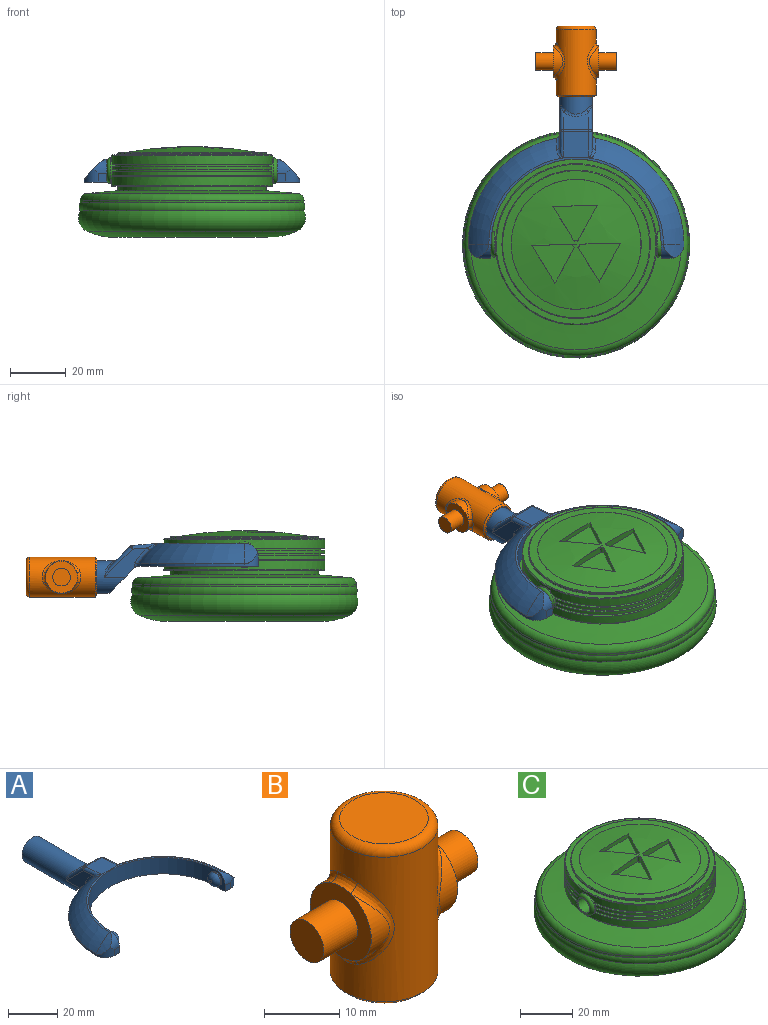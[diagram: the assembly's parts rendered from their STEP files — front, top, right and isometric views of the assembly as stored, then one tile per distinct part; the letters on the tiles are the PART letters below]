
ASSEMBLY  parts=3 mates=2
PART A: 48 faces, bbox 77.3x80.8x18.2 mm
  f0: plane 11.99x9.83mm, normal (0,-0.71,-0.71), area 141.5mm2, adj f1,f2,f9,f30,f43,f46
  f1: plane 15.39x10.49mm, normal (-1,0,0), area 63.5mm2, adj f0,f30,f32,f36,f46,f47
  f2: plane 15.39x10.49mm, normal (1,0,0), area 63.5mm2, adj f0,f30,f34,f39,f43,f44
  f3: plane 9.14x6.37mm, normal (0,0.71,0.71), area 67.6mm2, adj f35,f36,f39,f40
  f4: cylinder r=38.61mm len=37.99mm, axis (0,0,-1), area 42.6mm2, adj f6,f9,f17,f46,f47
  f5: torus R=19.3mm, axis (0,0,-1), area 507.8mm2, adj f10,f11,f12,f29,f42,f44
  f6: torus R=19.3mm, axis (0,0,-1), area 507.8mm2, adj f4,f11,f15,f28,f45,f47
  f7: cylinder r=30.48mm len=60.96mm, axis (0,0,-1), area 746.6mm2, adj f8,f9,f11,f14,f21,f24
  f8: plane 8.13x5.08mm, normal (-1,0,0), area 19.9mm2, adj f7,f9,f13,f19,f24
  f9: plane 77.22x43.73mm, normal (0,0,-1), area 956.2mm2, adj f0,f4,f7,f8,f10,f13,f14,f16
  f10: cylinder r=38.61mm len=37.99mm, axis (0,0,-1), area 42.6mm2, adj f5,f9,f20,f43,f44
  f11: plane 62.55x30.95mm, normal (0,0,1), area 75mm2, adj f5,f6,f7,f18,f19,f27
  f12: cylinder r=22.71mm len=7.33mm, axis (0,1,0), area 24.8mm2, adj f5,f19,f20
  f13: plane 3.05x3.05mm, normal (0,-1,0), area 9.3mm2, adj f8,f9,f19,f20
  f14: plane 8.13x5.08mm, normal (1,0,0), area 19.9mm2, adj f7,f9,f16,f18,f21
  f15: cylinder r=22.71mm len=7.33mm, axis (0,1,0), area 24.8mm2, adj f6,f17,f18
  f16: plane 3.05x3.05mm, normal (0,-1,0), area 9.3mm2, adj f9,f14,f17,f18
  f17: cylinder r=5.08mm len=5.08mm, axis (0,0,-1), area 21.9mm2, adj f4,f9,f15,f16,f18
  f18: cylinder r=5.08mm len=5.08mm, axis (-1,0,0), area 21.9mm2, adj f11,f14,f15,f16,f17
  f19: cylinder r=5.08mm len=5.08mm, axis (-1,0,0), area 21.9mm2, adj f8,f11,f12,f13,f20
  f20: cylinder r=5.08mm len=5.08mm, axis (0,0,-1), area 21.9mm2, adj f9,f10,f12,f13,f19
  f21: cylinder r=3.17mm len=6.35mm, axis (-1,0,0), area 12.7mm2, adj f7,f14,f23
  f22: plane 1.27x1.27mm, normal (1,0,0), area 1.3mm2, adj f23
  f23: torus R=0.64mm, axis (1,0,0), area 56.5mm2, adj f21,f22
  f24: cylinder r=3.17mm len=6.35mm, axis (1,0,0), area 12.7mm2, adj f7,f8,f26
  f25: plane 1.27x1.27mm, normal (-1,0,0), area 1.3mm2, adj f26
  f26: torus R=0.64mm, axis (-1,0,0), area 56.5mm2, adj f24,f25
  f27: plane 9.86x9.36mm, normal (0,0.09,1), area 85.6mm2, adj f11,f28,f29,f32,f34,f35,f42,f45
  f28: plane 1.04x0.17mm, normal (0,-1,0), area 0mm2, adj f6,f27,f45
  f29: plane 1.04x0.17mm, normal (0,-1,0), area 0mm2, adj f5,f27,f42
  f30: cylinder r=5.84mm len=33.01mm, axis (0,-1,0), area 1029.7mm2, adj f0,f1,f2,f31,f38,f40,f41
  f31: plane 11.68x11.68mm, normal (0,1,0), area 107.2mm2, adj f30
  f32: cylinder r=1.27mm len=9.13mm, axis (0,-1,0.09), area 14.4mm2, adj f1,f27,f33,f45
  f33: sphere r=1.27mm, area 1.5mm2, adj f32,f35,f36
  f34: cylinder r=1.27mm len=9.13mm, axis (0,1,-0.09), area 14.4mm2, adj f2,f27,f37,f42
  f35: cylinder r=1.27mm len=9.14mm, axis (-1,0,0), area 8.1mm2, adj f3,f27,f33,f37
  f36: cylinder r=1.27mm len=10.91mm, axis (0,-0.71,0.71), area 23.1mm2, adj f1,f3,f33,f38
  f37: sphere r=1.27mm, area 1.5mm2, adj f34,f35,f39
  f38: bspline ~4.55x2.75mm, area 2.3mm2, adj f30,f36,f40
  f39: cylinder r=1.27mm len=10.91mm, axis (0,0.71,-0.71), area 23.1mm2, adj f2,f3,f37,f41
  f40: bspline ~9.14x2.56mm, area 10.7mm2, adj f3,f30,f38,f41
  f41: bspline ~5.23x3.53mm, area 2.3mm2, adj f30,f39,f40
  f42: bspline ~4.62x3.14mm, area 5.2mm2, adj f5,f27,f29,f34,f44
  f43: cylinder r=1.27mm len=1.74mm, axis (0,0,-1), area 1.9mm2, adj f0,f2,f9,f10,f44
  f44: bspline ~8.6x7.86mm, area 11.9mm2, adj f2,f5,f10,f42,f43
  f45: bspline ~4.62x3.14mm, area 5.2mm2, adj f6,f27,f28,f32,f47
  f46: cylinder r=1.27mm len=1.74mm, axis (0,0,-1), area 1.9mm2, adj f0,f1,f4,f9,f47
  f47: bspline ~8.6x7.86mm, area 11.9mm2, adj f1,f4,f6,f45,f46
PART B: 25 faces, bbox 28.9x15.5x25.4 mm
  f0: cylinder r=5.71mm len=10.81mm, axis (-1,0,0), area 26.2mm2, adj f5,f15
  f1: cylinder r=5.71mm len=10.81mm, axis (-1,0,0), area 26.2mm2, adj f8,f11
  f2: cylinder r=7.14mm len=23.5mm, axis (0,0,-1), area 763.2mm2, adj f9,f10,f11,f12,f13,f14,f15,f16
  f3: plane 11.75x11.75mm, normal (0,0,1), area 108.4mm2, adj f17
  f4: plane 13.02x13.02mm, normal (0,0,-1), area 16.3mm2, adj f22,f24
  f5: plane 11.46x11.46mm, normal (1,0,0), area 70.9mm2, adj f0,f6,f13,f16,f18
  f6: cylinder r=5.71mm len=10.81mm, axis (-1,0,0), area 26.2mm2, adj f5,f14
  f7: cylinder r=5.71mm len=10.81mm, axis (-1,0,0), area 26.2mm2, adj f8,f10
  f8: plane 11.46x11.46mm, normal (-1,0,0), area 70.9mm2, adj f1,f7,f9,f12,f20
  f9: bspline ~4.64x1.73mm, area 6.5mm2, adj f2,f8,f10,f11
  f10: bspline ~13.62x4.91mm, area 20.7mm2, adj f2,f7,f9,f12
  f11: bspline ~13.6x4.87mm, area 20.7mm2, adj f1,f2,f9,f12
  f12: bspline ~4.64x1.73mm, area 6.5mm2, adj f2,f8,f10,f11
  f13: bspline ~4.64x1.73mm, area 6.5mm2, adj f2,f5,f14,f15
  f14: bspline ~13.62x4.91mm, area 20.7mm2, adj f2,f6,f13,f16
  f15: bspline ~13.6x4.87mm, area 20.7mm2, adj f0,f2,f13,f16
  f16: bspline ~4.64x1.73mm, area 6.5mm2, adj f2,f5,f14,f15
  f17: torus R=5.87mm, axis (0,0,1), area 83.8mm2, adj f2,f3
  f18: cylinder r=3.17mm len=6.35mm, axis (-1,0,0), area 126.7mm2, adj f5,f19
  f19: plane 6.35x6.35mm, normal (1,0,0), area 31.7mm2, adj f18
  f20: cylinder r=3.17mm len=6.35mm, axis (1,0,0), area 126.7mm2, adj f8,f21
  f21: plane 6.35x6.35mm, normal (-1,0,0), area 31.7mm2, adj f20
  f22: cylinder r=6.1mm len=22.86mm, axis (0,0,-1), area 875.6mm2, adj f4,f23
  f23: plane 12.19x12.19mm, normal (0,0,-1), area 116.7mm2, adj f22
  f24: cone r=7.14mm half-angle=45deg, axis (0,0,1), area 38.5mm2, adj f2,f4
PART C: 64 faces, bbox 96.3x96.3x32.5 mm
  f0: cylinder r=28.87mm len=57.73mm, axis (0,0,-1), area 543.4mm2, adj f3,f4,f54,f55,f60
  f1: plane 57.09x24.58mm, normal (0,0,-1), area 101.7mm2, adj f6,f7,f54,f55
  f2: plane 57.09x24.58mm, normal (0,0,-1), area 101.7mm2, adj f5,f8,f54,f55
  f3: plane 57.18x24.87mm, normal (0,0,1), area 102.5mm2, adj f0,f6,f54,f55
  f4: plane 57.18x24.87mm, normal (0,0,1), area 102.5mm2, adj f0,f5,f54,f55
  f5: cylinder r=27.6mm len=54.61mm, axis (0,0,1), area 49.8mm2, adj f2,f4,f54,f55
  f6: cylinder r=27.6mm len=54.61mm, axis (0,0,1), area 49.8mm2, adj f1,f3,f54,f55
  f7: cylinder r=28.87mm len=57.09mm, axis (0,0,-1), area 103.8mm2, adj f1,f9,f54,f55
  f8: cylinder r=28.87mm len=57.09mm, axis (0,0,-1), area 103.8mm2, adj f2,f10,f54,f55
  f9: plane 57.01x24.31mm, normal (0,0,1), area 101mm2, adj f7,f12,f54,f55
  f10: plane 57.01x24.31mm, normal (0,0,1), area 101mm2, adj f8,f11,f54,f55
  f11: cylinder r=27.6mm len=54.44mm, axis (0,0,1), area 49.2mm2, adj f10,f14,f54,f55
  f12: cylinder r=27.6mm len=54.44mm, axis (0,0,1), area 49.2mm2, adj f9,f13,f54,f55
  f13: plane 57.01x24.31mm, normal (0,0,-1), area 101mm2, adj f12,f15,f54,f55
  f14: plane 57.01x24.31mm, normal (0,0,-1), area 101mm2, adj f11,f16,f54,f55
  f15: cylinder r=28.87mm len=57.09mm, axis (0,0,-1), area 103.8mm2, adj f13,f19,f54,f55
  f16: cylinder r=28.87mm len=57.09mm, axis (0,0,-1), area 103.8mm2, adj f14,f20,f54,f55
  f17: plane 57.18x24.87mm, normal (0,0,-1), area 102.5mm2, adj f22,f23,f54,f55
  f18: plane 57.18x24.87mm, normal (0,0,-1), area 102.5mm2, adj f21,f23,f54,f55
  f19: plane 57.09x24.58mm, normal (0,0,1), area 101.7mm2, adj f15,f22,f54,f55
  f20: plane 57.09x24.58mm, normal (0,0,1), area 101.7mm2, adj f16,f21,f54,f55
  f21: cylinder r=27.6mm len=54.61mm, axis (0,0,1), area 49.8mm2, adj f18,f20,f54,f55
  f22: cylinder r=27.6mm len=54.61mm, axis (0,0,1), area 49.8mm2, adj f17,f19,f54,f55
  f23: cylinder r=28.87mm len=57.73mm, axis (0,0,-1), area 543.4mm2, adj f17,f18,f54,f55,f61
  f24: sphere r=135.39mm, area 1385.3mm2, adj f38,f39,f40,f41,f43,f44,f45,f46
  f25: plane 39.35x39.35mm, normal (0,0,-1), area 1216.2mm2, adj f26
  f26: torus R=20.13mm, axis (0,0,-1), area 1430.4mm2, adj f25,f27
  f27: torus R=27.75mm, axis (0,0,-1), area 3543.7mm2, adj f26,f28
  f28: torus R=35.37mm, axis (0,0,-1), area 2180.8mm2, adj f27,f29
  f29: torus R=37.36mm, axis (0,0,-1), area 734.8mm2, adj f28,f30
  f30: cylinder r=40.07mm len=80.14mm, axis (0,0,-1), area 213.4mm2, adj f29,f34
  f31: cone r=26.58mm half-angle=85deg, axis (0,0,-1), area 2265.9mm2, adj f32,f34
  f32: cylinder r=26.58mm len=53.16mm, axis (0,0,-1), area 265.1mm2, adj f31,f33
  f33: plane 57.23x57.23mm, normal (0,0,-1), area 352.3mm2, adj f32,f60
  f34: torus R=37.53mm, axis (0,0,1), area 928.9mm2, adj f30,f31
  f35: cone r=26.58mm half-angle=87deg, axis (0,0,-1), area 477.5mm2, adj f62,f63
  f36: cylinder r=26.58mm len=53.16mm, axis (0,0,-1), area 92.3mm2, adj f37,f62
  f37: plane 57.23x57.23mm, normal (0,0,1), area 352.3mm2, adj f36,f61
  f38: cylinder r=1.27mm len=2.53mm, axis (0,0,1), area 3.4mm2, adj f24,f39,f41,f42
  f39: plane 14.6x2.53mm, normal (0.03,-1,0), area 32.2mm2, adj f24,f38,f40,f42
  f40: plane 13.53x8.31mm, normal (0.85,0.52,0), area 28mm2, adj f24,f39,f41,f42
  f41: plane 12.84x6.95mm, normal (-0.88,0.48,0), area 32.2mm2, adj f24,f38,f40,f42
  f42: plane 15.26x13.93mm, normal (0,0,1), area 108.3mm2, adj f38,f39,f40,f41
  f43: cylinder r=1.27mm len=2.53mm, axis (0,0,1), area 3.4mm2, adj f24,f44,f46,f47
  f44: plane 12.44x7.65mm, normal (0.85,0.52,0), area 32.2mm2, adj f24,f43,f45,f47
  f45: plane 13.96x7.56mm, normal (-0.88,0.48,0), area 28mm2, adj f24,f44,f46,f47
  f46: plane 14.6x2.53mm, normal (0.03,-1,0), area 32.2mm2, adj f24,f43,f45,f47
  f47: plane 15.2x13.96mm, normal (0,0,1), area 108.3mm2, adj f43,f44,f45,f46
  f48: cylinder r=1.27mm len=2.53mm, axis (0,0,1), area 3.4mm2, adj f24,f49,f51,f52
  f49: plane 12.84x6.95mm, normal (-0.88,0.48,0), area 32.2mm2, adj f24,f48,f50,f52
  f50: plane 15.87x1.84mm, normal (0.03,-1,0), area 28mm2, adj f24,f49,f51,f52
  f51: plane 12.44x7.65mm, normal (0.85,0.52,0), area 32.2mm2, adj f24,f48,f50,f52
  f52: plane 15.87x12.88mm, normal (0,0,1), area 108.3mm2, adj f48,f49,f50,f51
  f53: plane 6.6x6.6mm, normal (1,0,0), area 2.6mm2, adj f58,f59
  f54: cylinder r=4.57mm len=9.14mm, axis (-1,0,0), area 20.3mm2, adj f0,f1,f2,f3,f4,f5,f6,f7
  f55: cylinder r=4.57mm len=9.14mm, axis (-1,0,0), area 20.3mm2, adj f0,f1,f2,f3,f4,f5,f6,f7
  f56: plane 6.6x6.6mm, normal (-1,0,0), area 2.6mm2, adj f57,f59
  f57: torus R=3.3mm, axis (1,0,0), area 51.5mm2, adj f55,f56
  f58: torus R=3.3mm, axis (1,0,0), area 51.5mm2, adj f53,f54
  f59: cylinder r=3.17mm len=60.96mm, axis (1,0,0), area 1216.1mm2, adj f53,f56
  f60: torus R=28.61mm, axis (0,0,1), area 72.1mm2, adj f0,f33
  f61: torus R=28.61mm, axis (0,0,-1), area 72.1mm2, adj f23,f37
  f62: torus R=26.33mm, axis (0,0,1), area 64.2mm2, adj f35,f36
  f63: torus R=23.29mm, axis (0,0,1), area 4.5mm2, adj f24,f35
PLACE A t=(32.34,27.52,20.85)mm
PLACE B rot(axis=(-1,0,0),90deg) t=(32.34,80.3,16.88)mm
PLACE C t=(32.34,27.52,33.52)mm
MATE revolute A.f24 <-> C.f54  axis (-1,0,0) through (62.82,27.52,24.92)mm
MATE revolute B.f2 <-> A.f30  axis (0,-1,0) through (32.34,103.16,16.88)mm
